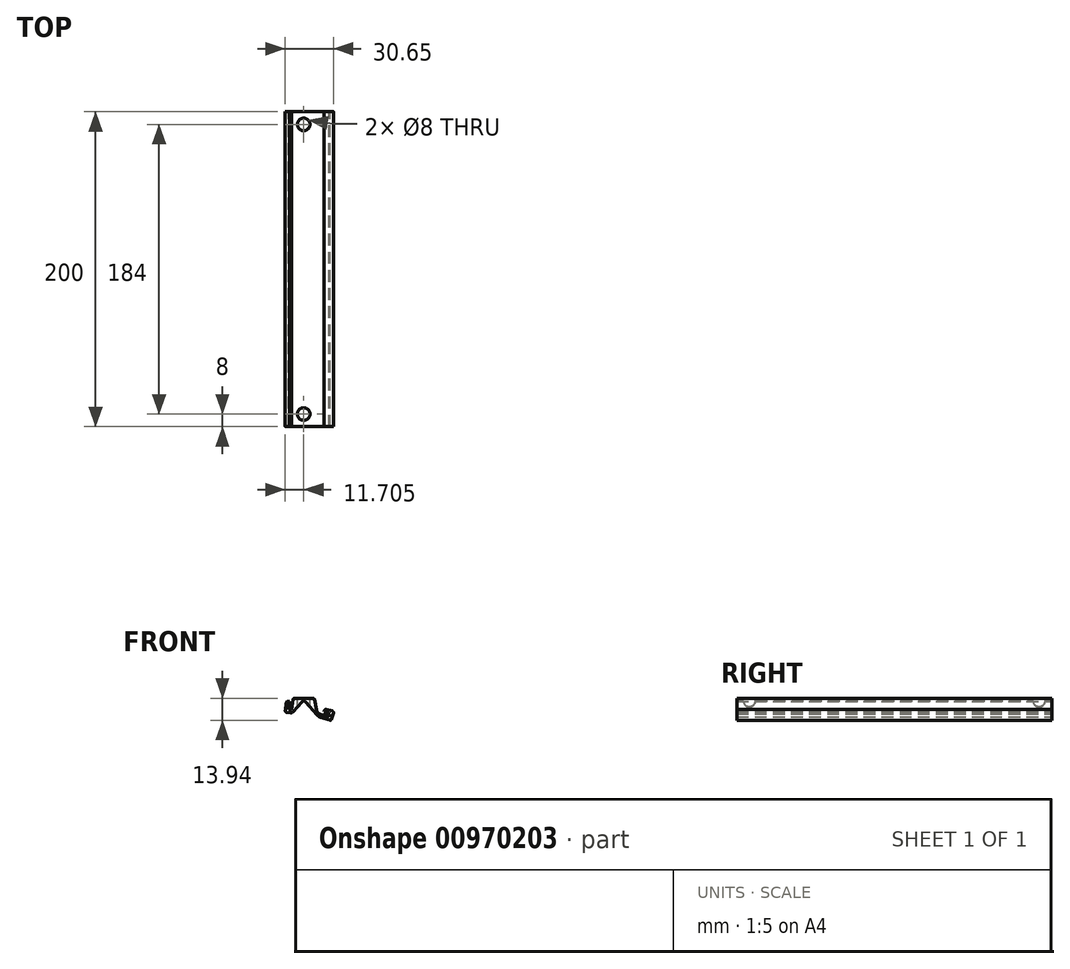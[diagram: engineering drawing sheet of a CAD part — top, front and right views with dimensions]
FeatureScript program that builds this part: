
annotation { "Feature Type Name" : "Feature", "Feature Type Description" : "" }
export const myFeature = defineFeature(function(context is Context, id is Id, definition is map)
    precondition{}
    {
        {
            var Q0;
            Q0=qCreatedBy(makeId("Front.planeOp"),FACE);
            var sketch = newSketch(context, id + "F0", { "sketchPlane" : qUnion([Q0])});
            skPoint(sketch, "E0.end.orphan", {"position": v(9.12, 0) * mm});
            skLineSegment(sketch, "E1", {"start": v(0, 0) * mm, "end": v(0.83, 6.62) * mm});
            skLineSegment(sketch, "E2", {"start": v(2.32, 7.94) * mm, "end": v(14.37, 7.94) * mm});
            skLineSegment(sketch, "E3", {"start": v(16.33, 6.34) * mm, "end": v(17.7, -0.4) * mm});
            skLineSegment(sketch, "E4", {"start": v(19.44, -2.29) * mm, "end": v(24.7, -3.86) * mm});
            skPoint(sketch, "E5.visualSharp", {"position": v(1, 7.94) * mm});
            skArc(sketch, "E5.filletArc", {"start": v(2.32, 7.94) * mm, "mid": v(1.33, 7.56) * mm, "end": v(0.83, 6.62) * mm});
            skPoint(sketch, "E6.visualSharp", {"position": v(16, 7.94) * mm});
            skArc(sketch, "E6.filletArc", {"start": v(16.33, 6.34) * mm, "mid": v(15.63, 7.49) * mm, "end": v(14.37, 7.94) * mm});
            skPoint(sketch, "E7.visualSharp", {"position": v(18, -1.86) * mm});
            skArc(sketch, "E7.filletArc", {"start": v(17.7, -0.4) * mm, "mid": v(18.3, -1.58) * mm, "end": v(19.44, -2.29) * mm});
            skLineSegment(sketch, "E8.0", {"start": v(19.22, -3) * mm, "end": v(24.5, -4.58) * mm});
            skLineSegment(sketch, "E8.1", {"start": v(0.74, -0.1) * mm, "end": v(1.55, 6.31) * mm});
            skLineSegment(sketch, "E8.2", {"start": v(2.54, 7.19) * mm, "end": v(14.16, 7.19) * mm});
            skLineSegment(sketch, "E8.3", {"start": v(15.63, 5.99) * mm, "end": v(16.97, -0.54) * mm});
            skArc(sketch, "E8.4", {"start": v(16.97, -0.54) * mm, "mid": v(17.75, -2.09) * mm, "end": v(19.22, -3) * mm});
            skLineSegment(sketch, "E9.0", {"start": v(19.8, -1.61) * mm, "end": v(24.92, -3.14) * mm});
            skLineSegment(sketch, "E9.1", {"start": v(17.06, 6.49) * mm, "end": v(18.4, -0.1) * mm});
            skLineSegment(sketch, "E9.2", {"start": v(-0.74, 0.1) * mm, "end": v(0.1, 6.72) * mm});
            skArc(sketch, "E9.3", {"start": v(2.32, 8.69) * mm, "mid": v(0.83, 8.12) * mm, "end": v(0.1, 6.72) * mm});
            skLineSegment(sketch, "E9.4", {"start": v(2.32, 8.69) * mm, "end": v(14.37, 8.69) * mm});
            skArc(sketch, "E9.5", {"start": v(17.06, 6.49) * mm, "mid": v(16.1, 8.07) * mm, "end": v(14.37, 8.69) * mm});
            skLineSegment(sketch, "E10", {"start": v(-0.74, 0.1) * mm, "end": v(0.74, -0.1) * mm});
            skLineSegment(sketch, "E11", {"start": v(24.5, -4.58) * mm, "end": v(24.92, -3.14) * mm});
            skPoint(sketch, "E12.visualSharp", {"position": v(1.66, 7.19) * mm});
            skArc(sketch, "E12.filletArc", {"start": v(2.54, 7.19) * mm, "mid": v(1.88, 6.94) * mm, "end": v(1.55, 6.31) * mm});
            skPoint(sketch, "E13.visualSharp", {"position": v(15.39, 7.19) * mm});
            skArc(sketch, "E13.filletArc", {"start": v(15.63, 5.99) * mm, "mid": v(15.11, 6.85) * mm, "end": v(14.16, 7.19) * mm});
            skPoint(sketch, "E14.visualSharp", {"position": v(18.64, -1.27) * mm});
            skArc(sketch, "E14.filletArc", {"start": v(18.4, -0.1) * mm, "mid": v(18.89, -1.05) * mm, "end": v(19.8, -1.61) * mm});
            skLineSegment(sketch, "E15.0", {"start": v(19.15, -3.25) * mm, "end": v(24.42, -4.82) * mm});
            skLineSegment(sketch, "E15.1", {"start": v(1, -0.13) * mm, "end": v(1.77, 6.06) * mm});
            skLineSegment(sketch, "E15.2", {"start": v(2.76, 6.94) * mm, "end": v(14.37, 6.94) * mm});
            skLineSegment(sketch, "E15.3", {"start": v(15.35, 6.14) * mm, "end": v(16.72, -0.6) * mm});
            skArc(sketch, "E15.4", {"start": v(16.72, -0.6) * mm, "mid": v(17.57, -2.26) * mm, "end": v(19.15, -3.25) * mm});
            skLineSegment(sketch, "E16", {"start": v(24.42, -4.82) * mm, "end": v(24.66, -4.9) * mm});
            skLineSegment(sketch, "E17", {"start": v(24.66, -4.9) * mm, "end": v(25.23, -2.97) * mm});
            skLineSegment(sketch, "E18", {"start": v(-1.02, -0.12) * mm, "end": v(0.96, -0.37) * mm});
            skLineSegment(sketch, "E19", {"start": v(1, -0.13) * mm, "end": v(0.96, -0.37) * mm});
            skPoint(sketch, "E20.visualSharp", {"position": v(1.88, 6.94) * mm});
            skArc(sketch, "E20.filletArc", {"start": v(2.76, 6.94) * mm, "mid": v(2.1, 6.69) * mm, "end": v(1.77, 6.06) * mm});
            skLineSegment(sketch, "E21", {"start": v(25.23, -2.97) * mm, "end": v(22.69, -2.22) * mm});
            skLineSegment(sketch, "E22", {"start": v(-1.02, -0.12) * mm, "end": v(-0.4, 4.84) * mm});
            skLineSegment(sketch, "E23", {"start": v(22.69, -2.22) * mm, "end": v(21.4, -1.83) * mm});
            skPoint(sketch, "E24.visualSharp", {"position": v(15.18, 6.94) * mm});
            skArc(sketch, "E24.filletArc", {"start": v(15.35, 6.14) * mm, "mid": v(15, 6.71) * mm, "end": v(14.37, 6.94) * mm});
            skPoint(sketch, "E25", {"position": v(8.57, 6.94) * mm});
            skPoint(sketch, "E26", {"position": v(8.57, 5.94) * mm});
            skLineSegment(sketch, "E27", {"start": v(-1.64, -2.06) * mm, "end": v(0.16, -2.29) * mm});
            skLineSegment(sketch, "E28", {"start": v(1.9, -1.62) * mm, "end": v(7.44, 4.65) * mm});
            skLineSegment(sketch, "E29", {"start": v(19.37, -5.26) * mm, "end": v(25.09, -6.96) * mm});
            skLineSegment(sketch, "E30", {"start": v(9.7, 4.65) * mm, "end": v(17.03, -3.76) * mm});
            skLineSegment(sketch, "E31", {"start": v(-0.4, 4.84) * mm, "end": v(-1.4, 4.96) * mm});
            skLineSegment(sketch, "E32", {"start": v(-2.5, 4.1) * mm, "end": v(-3.13, -0.87) * mm});
            skLineSegment(sketch, "E33", {"start": v(-1.64, -2.06) * mm, "end": v(-2.27, -1.98) * mm});
            skLineSegment(sketch, "E34", {"start": v(26.33, -6.3) * mm, "end": v(27.47, -2.48) * mm});
            skLineSegment(sketch, "E35", {"start": v(21.4, -1.83) * mm, "end": v(21.7, -0.85) * mm});
            skLineSegment(sketch, "E36", {"start": v(22.91, -0.17) * mm, "end": v(26.77, -1.23) * mm});
            skPoint(sketch, "E37.visualSharp", {"position": v(26.05, -7.25) * mm});
            skArc(sketch, "E37.filletArc", {"start": v(25.09, -6.96) * mm, "mid": v(25.85, -6.88) * mm, "end": v(26.33, -6.3) * mm});
            skPoint(sketch, "E38.visualSharp", {"position": v(27.76, -1.5) * mm});
            skArc(sketch, "E38.filletArc", {"start": v(27.47, -2.48) * mm, "mid": v(27.38, -1.7) * mm, "end": v(26.77, -1.23) * mm});
            skPoint(sketch, "E39.visualSharp", {"position": v(21.97, 0.09) * mm});
            skArc(sketch, "E39.filletArc", {"start": v(22.91, -0.17) * mm, "mid": v(22.17, -0.26) * mm, "end": v(21.7, -0.85) * mm});
            skPoint(sketch, "E40.visualSharp", {"position": v(-3.26, -1.86) * mm});
            skArc(sketch, "E40.filletArc", {"start": v(-3.13, -0.87) * mm, "mid": v(-2.93, -1.6) * mm, "end": v(-2.27, -1.98) * mm});
            skPoint(sketch, "E41.visualSharp", {"position": v(-2.38, 5.09) * mm});
            skArc(sketch, "E41.filletArc", {"start": v(-1.4, 4.96) * mm, "mid": v(-2.13, 4.76) * mm, "end": v(-2.5, 4.1) * mm});
            skPoint(sketch, "E42.visualSharp", {"position": v(1.2, -2.42) * mm});
            skArc(sketch, "E42.filletArc", {"start": v(0.16, -2.29) * mm, "mid": v(1.11, -2.17) * mm, "end": v(1.9, -1.62) * mm});
            skPoint(sketch, "E43.visualSharp", {"position": v(17.98, -4.84) * mm});
            skArc(sketch, "E43.filletArc", {"start": v(17.03, -3.76) * mm, "mid": v(18.1, -4.67) * mm, "end": v(19.37, -5.26) * mm});
            skArc(sketch, "E44.filletArc", {"start": v(9.7, 4.65) * mm, "mid": v(8.56, 5.16) * mm, "end": v(7.44, 4.65) * mm});
            skSolve(sketch);
        }
        {
            var Q0;
            Q0=makeQuery(id+"F0.imprint","IMPRINT",FACE,{"disambiguationData":[TD([[makeQuery(id+"F0.imprint","IMPRINT",EDGE,{"derivedFrom":sQuery(id+"F0.wireOp",EDGE,"E15.0")}),-1.0]])]});
            extrude(context, id + "F1", {"entities" : qUnion([Q0]), "depth" : 100 * mm, "offsetDistance" : 25 * mm, "hasSecondDirection" : true, "secondDirectionOppositeDirection" : true, "secondDirectionDepth" : 100 * mm});
        }
        {
            var Q0;
            Q0=makeQuery(id+"F1.opExtrude","SWEPT_FACE",FACE,{"disambiguationData":[OSD([sQuery(id+"F0.wireOp",EDGE,"E15.2")])]});
            var sketch = newSketch(context, id + "F2", { "sketchPlane" : qUnion([Q0])});
            skLineSegment(sketch, "E45.0", {"start": v(2.76, 100) * mm, "end": v(14.37, 100) * mm});
            skLineSegment(sketch, "E46.0", {"start": v(2.76, -100) * mm, "end": v(14.37, -100) * mm});
            skPoint(sketch, "E47", {"position": v(8.57, -92) * mm});
            skPoint(sketch, "E47.positionSnap0", {"position": v(8.57, -100) * mm});
            skPoint(sketch, "E48", {"position": v(8.57, 92) * mm});
            skPoint(sketch, "E48.positionSnap0", {"position": v(8.57, 100) * mm});
            skCircle(sketch, "E49", {"center": v(8.57, -92) * mm, "radius": 4 * mm});
            skCircle(sketch, "E50", {"center": v(8.57, 92) * mm, "radius": 4 * mm});
            skSolve(sketch);
        }
        {
            var Q0;
            Q0=makeQuery(id+"F2.imprint","IMPRINT",FACE,{"disambiguationData":[TD([[makeQuery(id+"F2.imprint","IMPRINT",EDGE,{"derivedFrom":sQuery(id+"F2.wireOp",EDGE,"E49")}),1.0]])]});
            var Q1;
            Q1=makeQuery(id+"F2.imprint","IMPRINT",FACE,{"disambiguationData":[TD([[makeQuery(id+"F2.imprint","IMPRINT",EDGE,{"derivedFrom":sQuery(id+"F2.wireOp",EDGE,"E50")}),1.0]])]});
            extrude(context, id + "F3", {"entities" : qUnion([Q0, Q1]), "operationType" : NewBodyOperationType.REMOVE, "oppositeDirection" : true, "depth" : 25 * mm, "offsetDistance" : 25 * mm});
        }
    });
